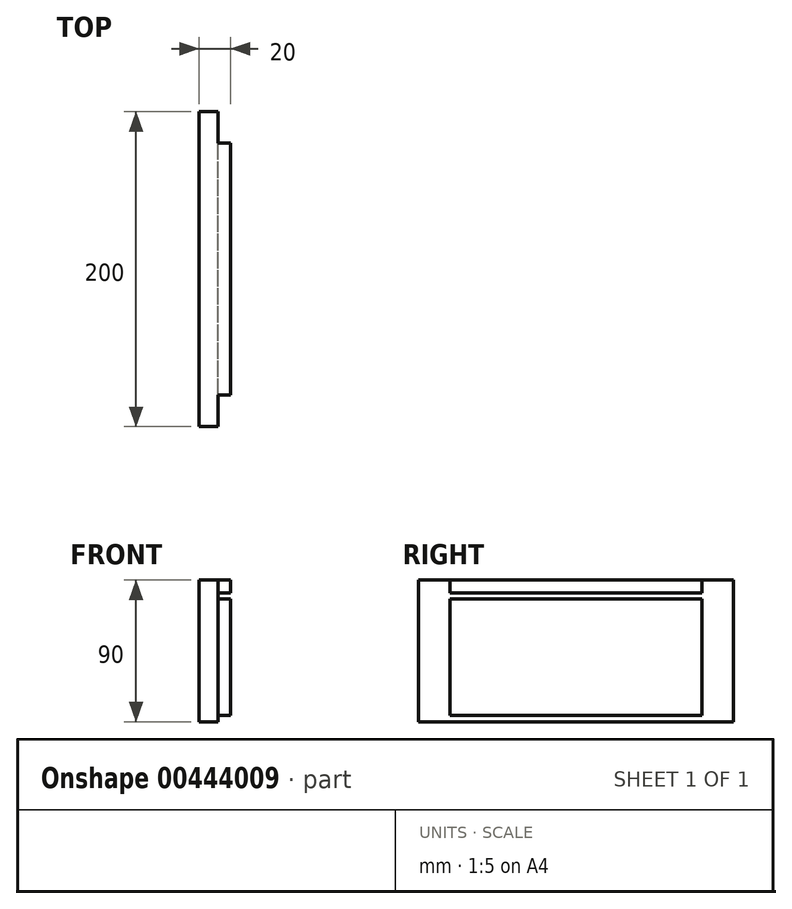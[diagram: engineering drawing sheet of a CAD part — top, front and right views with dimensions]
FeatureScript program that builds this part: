
annotation { "Feature Type Name" : "Feature", "Feature Type Description" : "" }
export const myFeature = defineFeature(function(context is Context, id is Id, definition is map)
    precondition{}
    {
        {
            var Q0;
            Q0=qCreatedBy(makeId("Right.planeOp"),FACE);
            var sketch = newSketch(context, id + "F0", { "sketchPlane" : qUnion([Q0])});
            skLineSegment(sketch, "E0.bottom", {"start": v(-101.64, 53.2) * mm, "end": v(98.36, 53.2) * mm});
            skLineSegment(sketch, "E0.top", {"start": v(-101.64, -36.8) * mm, "end": v(98.36, -36.8) * mm});
            skLineSegment(sketch, "E0.left", {"start": v(-101.64, 53.2) * mm, "end": v(-101.64, -36.8) * mm});
            skLineSegment(sketch, "E0.right", {"start": v(98.36, 53.2) * mm, "end": v(98.36, -36.8) * mm});
            skLineSegment(sketch, "E1", {"start": v(-81.64, 53.2) * mm, "end": v(-81.64, 45.2) * mm});
            skLineSegment(sketch, "E2", {"start": v(-81.64, 45.2) * mm, "end": v(78.36, 45.2) * mm});
            skLineSegment(sketch, "E3", {"start": v(78.36, 45.2) * mm, "end": v(78.36, 53.2) * mm});
            skLineSegment(sketch, "E4.bottom", {"start": v(-81.64, 41.2) * mm, "end": v(78.36, 41.2) * mm});
            skLineSegment(sketch, "E4.top", {"start": v(-81.64, -32.8) * mm, "end": v(78.36, -32.8) * mm});
            skLineSegment(sketch, "E4.left", {"start": v(-81.64, 41.2) * mm, "end": v(-81.64, -32.8) * mm});
            skLineSegment(sketch, "E4.right", {"start": v(78.36, 41.2) * mm, "end": v(78.36, -32.8) * mm});
            skSolve(sketch);
        }
        {
            var Q0;
            Q0=makeQuery(id+"F0.imprint","IMPRINT",FACE,{"disambiguationData":[TD([[makeQuery(id+"F0.imprint","IMPRINT",EDGE,{"derivedFrom":sQuery(id+"F0.wireOp",EDGE,"E4.bottom")}),-1.0]])]});
            extrude(context, id + "F1", {"entities" : qUnion([Q0]), "depth" : 20 * mm});
        }
        {
            var Q0;
            Q0=makeQuery(id+"F0.imprint","IMPRINT",FACE,{"disambiguationData":[TD([[makeQuery(id+"F0.imprint","IMPRINT",EDGE,{"derivedFrom":sQuery(id+"F0.wireOp",EDGE,"E0.top")}),1.0]])]});
            extrude(context, id + "F2", {"entities" : qUnion([Q0]), "operationType" : NewBodyOperationType.ADD, "depth" : 12 * mm});
        }
        {
            var Q0;
            {var subQ0=sQuery(id+"F0.wireOp",EDGE,"E1");Q0=makeQuery(id+"F0.imprint","IMPRINT",FACE,{"disambiguationData":[TD([[makeQuery(id+"F0.imprint","IMPRINT",EDGE,{"derivedFrom":subQ0}),1.0]])]});}
            extrude(context, id + "F3", {"entities" : qUnion([Q0]), "operationType" : NewBodyOperationType.ADD, "depth" : 20 * mm});
        }
    });
